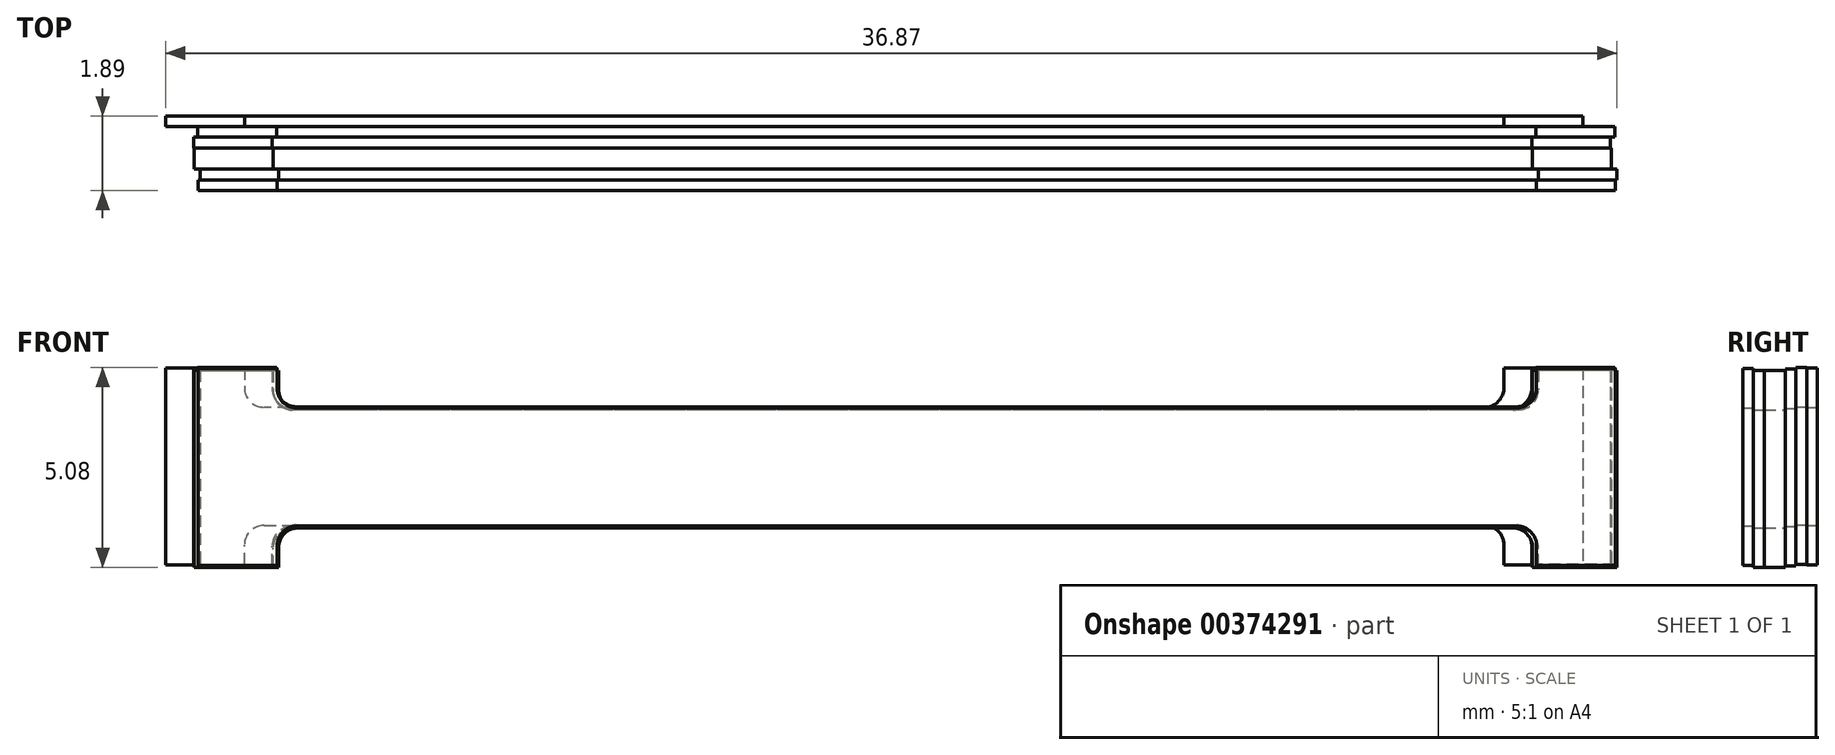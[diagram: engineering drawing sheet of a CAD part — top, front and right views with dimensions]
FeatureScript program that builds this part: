
annotation { "Feature Type Name" : "Feature", "Feature Type Description" : "" }
export const myFeature = defineFeature(function(context is Context, id is Id, definition is map)
    precondition{}
    {
        {
            var Q0;
            Q0=qCreatedBy(makeId("Front.planeOp"),FACE);
            var sketch = newSketch(context, id + "F0", { "sketchPlane" : qUnion([Q0])});
            skLineSegment(sketch, "E0", {"start": v(-18, 2.5) * mm, "end": v(-18, 0) * mm});
            skLineSegment(sketch, "E1", {"start": v(-18, 2.5) * mm, "end": v(-16, 2.5) * mm});
            skLineSegment(sketch, "E2", {"start": v(-18, 0) * mm, "end": v(18, 0) * mm});
            skLineSegment(sketch, "E3", {"start": v(-16, 2.5) * mm, "end": v(-16, 2) * mm});
            skLineSegment(sketch, "E4", {"start": v(-15.5, 1.5) * mm, "end": v(0, 1.5) * mm});
            skPoint(sketch, "E5.visualSharp", {"position": v(-16, 1.5) * mm});
            skArc(sketch, "E5.filletArc", {"start": v(-16, 2) * mm, "mid": v(-15.85, 1.65) * mm, "end": v(-15.5, 1.5) * mm});
            skLineSegment(sketch, "E6.MirrorCS", {"start": v(15.5, 1.5) * mm, "end": v(0, 1.5) * mm});
            skArc(sketch, "E7.MirrorCS", {"start": v(16, 2) * mm, "mid": v(15.85, 1.65) * mm, "end": v(15.5, 1.5) * mm});
            skLineSegment(sketch, "E8.MirrorCS", {"start": v(16, 2.5) * mm, "end": v(16, 2) * mm});
            skLineSegment(sketch, "E9.MirrorCS", {"start": v(18, 2.5) * mm, "end": v(16, 2.5) * mm});
            skLineSegment(sketch, "E10.MirrorCS", {"start": v(18, 2.5) * mm, "end": v(18, 0) * mm});
            skLineSegment(sketch, "E11.MirrorCS", {"start": v(-18, -2.5) * mm, "end": v(-18, 0) * mm});
            skLineSegment(sketch, "E12.MirrorCS", {"start": v(-18, -2.5) * mm, "end": v(-16, -2.5) * mm});
            skLineSegment(sketch, "E13.MirrorCS", {"start": v(-16, -2.5) * mm, "end": v(-16, -2) * mm});
            skArc(sketch, "E14.MirrorCS", {"start": v(-16, -2) * mm, "mid": v(-15.85, -1.65) * mm, "end": v(-15.5, -1.5) * mm});
            skLineSegment(sketch, "E15.MirrorCS", {"start": v(-15.5, -1.5) * mm, "end": v(0, -1.5) * mm});
            skLineSegment(sketch, "E16.MirrorCS", {"start": v(15.5, -1.5) * mm, "end": v(0, -1.5) * mm});
            skArc(sketch, "E17.MirrorCS", {"start": v(16, -2) * mm, "mid": v(15.85, -1.65) * mm, "end": v(15.5, -1.5) * mm});
            skLineSegment(sketch, "E18.MirrorCS", {"start": v(16, -2.5) * mm, "end": v(16, -2) * mm});
            skLineSegment(sketch, "E19.MirrorCS", {"start": v(18, -2.5) * mm, "end": v(16, -2.5) * mm});
            skLineSegment(sketch, "E20.MirrorCS", {"start": v(18, -2.5) * mm, "end": v(18, 0) * mm});
            skSolve(sketch);
        }
        {
            var Q0;
            Q0=qSketchRegion(id+"F0",true);
            extrude(context, id + "F1", {"entities" : qUnion([Q0]), "depth" : 0.27 * mm});
        }
        {
            var Q0;
            Q0=qCreatedBy(makeId("Front.planeOp"),FACE);
            cPlane(context, id + "F2", {"entities" : qUnion([Q0]), "cplaneType" : CPlaneType.OFFSET, "offset" : 0.27 * mm, "width" : 150 * mm, "height" : 150 * mm});
        }
        {
            var Q0;
            Q0=qCreatedBy(id+"F2.planeOp",FACE);
            var sketch = newSketch(context, id + "F3", { "sketchPlane" : qUnion([Q0])});
            skLineSegment(sketch, "E21", {"start": v(-17.18, 2.51) * mm, "end": v(-17.18, 0.01) * mm});
            skLineSegment(sketch, "E22", {"start": v(-17.18, 2.51) * mm, "end": v(-15.18, 2.51) * mm});
            skLineSegment(sketch, "E23", {"start": v(-17.18, 0.01) * mm, "end": v(18.82, 0.01) * mm});
            skLineSegment(sketch, "E24", {"start": v(-15.18, 2.51) * mm, "end": v(-15.18, 2.01) * mm});
            skLineSegment(sketch, "E25", {"start": v(-14.68, 1.51) * mm, "end": v(0.82, 1.51) * mm});
            skPoint(sketch, "E26.visualSharp", {"position": v(-15.18, 1.51) * mm});
            skArc(sketch, "E26.filletArc", {"start": v(-15.18, 2.01) * mm, "mid": v(-15.04, 1.66) * mm, "end": v(-14.68, 1.51) * mm});
            skLineSegment(sketch, "E27.MirrorCS", {"start": v(16.32, 1.51) * mm, "end": v(0.82, 1.51) * mm});
            skArc(sketch, "E28.MirrorCS", {"start": v(16.82, 2.01) * mm, "mid": v(16.67, 1.66) * mm, "end": v(16.32, 1.51) * mm});
            skLineSegment(sketch, "E29.MirrorCS", {"start": v(16.82, 2.51) * mm, "end": v(16.82, 2.01) * mm});
            skLineSegment(sketch, "E30.MirrorCS", {"start": v(18.82, 2.51) * mm, "end": v(16.82, 2.51) * mm});
            skLineSegment(sketch, "E31.MirrorCS", {"start": v(18.82, 2.51) * mm, "end": v(18.82, 0.01) * mm});
            skLineSegment(sketch, "E32.MirrorCS", {"start": v(-17.18, -2.49) * mm, "end": v(-17.18, 0.01) * mm});
            skLineSegment(sketch, "E33.MirrorCS", {"start": v(-17.18, -2.49) * mm, "end": v(-15.18, -2.49) * mm});
            skLineSegment(sketch, "E34.MirrorCS", {"start": v(-15.18, -2.49) * mm, "end": v(-15.18, -1.99) * mm});
            skArc(sketch, "E35.MirrorCS", {"start": v(-15.18, -1.99) * mm, "mid": v(-15.04, -1.63) * mm, "end": v(-14.68, -1.49) * mm});
            skLineSegment(sketch, "E36.MirrorCS", {"start": v(-14.68, -1.49) * mm, "end": v(0.82, -1.49) * mm});
            skLineSegment(sketch, "E37.MirrorCS", {"start": v(16.32, -1.49) * mm, "end": v(0.82, -1.49) * mm});
            skArc(sketch, "E38.MirrorCS", {"start": v(16.82, -1.99) * mm, "mid": v(16.67, -1.63) * mm, "end": v(16.32, -1.49) * mm});
            skLineSegment(sketch, "E39.MirrorCS", {"start": v(16.82, -2.49) * mm, "end": v(16.82, -1.99) * mm});
            skLineSegment(sketch, "E40.MirrorCS", {"start": v(18.82, -2.49) * mm, "end": v(16.82, -2.49) * mm});
            skLineSegment(sketch, "E41.MirrorCS", {"start": v(18.82, -2.49) * mm, "end": v(18.82, 0.01) * mm});
            skSolve(sketch);
        }
        {
            var Q0;
            Q0=qSketchRegion(id+"F3",true);
            extrude(context, id + "F4", {"entities" : qUnion([Q0]), "operationType" : NewBodyOperationType.REMOVE, "depth" : 0.27 * mm});
        }
        {
            var Q0;
            Q0=qCreatedBy(id+"F2.planeOp",FACE);
            cPlane(context, id + "F5", {"entities" : qUnion([Q0]), "cplaneType" : CPlaneType.OFFSET, "offset" : 0.27 * mm, "width" : 150 * mm, "height" : 150 * mm});
        }
        {
            var Q0;
            Q0=qCreatedBy(id+"F5.planeOp",FACE);
            var sketch = newSketch(context, id + "F6", { "sketchPlane" : qUnion([Q0])});
            skLineSegment(sketch, "E42", {"start": v(-17.3, 2.47) * mm, "end": v(-17.3, -0.03) * mm});
            skLineSegment(sketch, "E43", {"start": v(-17.3, 2.47) * mm, "end": v(-15.3, 2.47) * mm});
            skLineSegment(sketch, "E44", {"start": v(-17.3, -0.03) * mm, "end": v(18.7, -0.03) * mm});
            skLineSegment(sketch, "E45", {"start": v(-15.3, 2.47) * mm, "end": v(-15.3, 1.97) * mm});
            skLineSegment(sketch, "E46", {"start": v(-14.8, 1.47) * mm, "end": v(0.7, 1.47) * mm});
            skPoint(sketch, "E47.visualSharp", {"position": v(-15.3, 1.47) * mm});
            skArc(sketch, "E47.filletArc", {"start": v(-15.3, 1.97) * mm, "mid": v(-15.15, 1.62) * mm, "end": v(-14.8, 1.47) * mm});
            skLineSegment(sketch, "E48.MirrorCS", {"start": v(16.2, 1.47) * mm, "end": v(0.7, 1.47) * mm});
            skArc(sketch, "E49.MirrorCS", {"start": v(16.7, 1.97) * mm, "mid": v(16.56, 1.62) * mm, "end": v(16.2, 1.47) * mm});
            skLineSegment(sketch, "E50.MirrorCS", {"start": v(16.7, 2.47) * mm, "end": v(16.7, 1.97) * mm});
            skLineSegment(sketch, "E51.MirrorCS", {"start": v(18.7, 2.47) * mm, "end": v(16.7, 2.47) * mm});
            skLineSegment(sketch, "E52.MirrorCS", {"start": v(18.7, 2.47) * mm, "end": v(18.7, -0.03) * mm});
            skLineSegment(sketch, "E53.MirrorCS", {"start": v(-17.3, -2.53) * mm, "end": v(-17.3, -0.03) * mm});
            skLineSegment(sketch, "E54.MirrorCS", {"start": v(-17.3, -2.53) * mm, "end": v(-15.3, -2.53) * mm});
            skLineSegment(sketch, "E55.MirrorCS", {"start": v(-15.3, -2.53) * mm, "end": v(-15.3, -2.03) * mm});
            skArc(sketch, "E56.MirrorCS", {"start": v(-15.3, -2.03) * mm, "mid": v(-15.15, -1.67) * mm, "end": v(-14.8, -1.53) * mm});
            skLineSegment(sketch, "E57.MirrorCS", {"start": v(-14.8, -1.53) * mm, "end": v(0.7, -1.53) * mm});
            skLineSegment(sketch, "E58.MirrorCS", {"start": v(16.2, -1.53) * mm, "end": v(0.7, -1.53) * mm});
            skArc(sketch, "E59.MirrorCS", {"start": v(16.7, -2.03) * mm, "mid": v(16.56, -1.67) * mm, "end": v(16.2, -1.53) * mm});
            skLineSegment(sketch, "E60.MirrorCS", {"start": v(16.7, -2.53) * mm, "end": v(16.7, -2.03) * mm});
            skLineSegment(sketch, "E61.MirrorCS", {"start": v(18.7, -2.53) * mm, "end": v(16.7, -2.53) * mm});
            skLineSegment(sketch, "E62.MirrorCS", {"start": v(18.7, -2.53) * mm, "end": v(18.7, -0.03) * mm});
            skSolve(sketch);
        }
        {
            var Q0;
            Q0=qSketchRegion(id+"F6",true);
            extrude(context, id + "F7", {"entities" : qUnion([Q0]), "operationType" : NewBodyOperationType.ADD, "depth" : 0.27 * mm});
        }
        {
            var Q0;
            Q0=qCreatedBy(id+"F5.planeOp",FACE);
            cPlane(context, id + "F8", {"entities" : qUnion([Q0]), "cplaneType" : CPlaneType.OFFSET, "offset" : 0.27 * mm, "width" : 150 * mm, "height" : 150 * mm});
        }
        {
            var Q0;
            Q0=qCreatedBy(id+"F8.planeOp",FACE);
            var sketch = newSketch(context, id + "F9", { "sketchPlane" : qUnion([Q0])});
            skLineSegment(sketch, "E63", {"start": v(-17.25, 2.45) * mm, "end": v(-17.25, -0.05) * mm});
            skLineSegment(sketch, "E64", {"start": v(-17.25, 2.45) * mm, "end": v(-15.25, 2.45) * mm});
            skLineSegment(sketch, "E65", {"start": v(-17.25, -0.05) * mm, "end": v(18.75, -0.05) * mm});
            skLineSegment(sketch, "E66", {"start": v(-15.25, 2.45) * mm, "end": v(-15.25, 1.95) * mm});
            skLineSegment(sketch, "E67", {"start": v(-14.75, 1.45) * mm, "end": v(0.75, 1.45) * mm});
            skPoint(sketch, "E68.visualSharp", {"position": v(-15.25, 1.45) * mm});
            skArc(sketch, "E68.filletArc", {"start": v(-15.25, 1.95) * mm, "mid": v(-15.1, 1.6) * mm, "end": v(-14.75, 1.45) * mm});
            skLineSegment(sketch, "E69.MirrorCS", {"start": v(16.25, 1.45) * mm, "end": v(0.75, 1.45) * mm});
            skArc(sketch, "E70.MirrorCS", {"start": v(16.75, 1.95) * mm, "mid": v(16.6, 1.6) * mm, "end": v(16.25, 1.45) * mm});
            skLineSegment(sketch, "E71.MirrorCS", {"start": v(16.75, 2.45) * mm, "end": v(16.75, 1.95) * mm});
            skLineSegment(sketch, "E72.MirrorCS", {"start": v(18.75, 2.45) * mm, "end": v(16.75, 2.45) * mm});
            skLineSegment(sketch, "E73.MirrorCS", {"start": v(18.75, 2.45) * mm, "end": v(18.75, -0.05) * mm});
            skLineSegment(sketch, "E74.MirrorCS", {"start": v(-17.25, -2.55) * mm, "end": v(-17.25, -0.05) * mm});
            skLineSegment(sketch, "E75.MirrorCS", {"start": v(-17.25, -2.55) * mm, "end": v(-15.25, -2.55) * mm});
            skLineSegment(sketch, "E76.MirrorCS", {"start": v(-15.25, -2.55) * mm, "end": v(-15.25, -2.05) * mm});
            skArc(sketch, "E77.MirrorCS", {"start": v(-15.25, -2.05) * mm, "mid": v(-15.1, -1.7) * mm, "end": v(-14.75, -1.55) * mm});
            skLineSegment(sketch, "E78.MirrorCS", {"start": v(-14.75, -1.55) * mm, "end": v(0.75, -1.55) * mm});
            skLineSegment(sketch, "E79.MirrorCS", {"start": v(16.25, -1.55) * mm, "end": v(0.75, -1.55) * mm});
            skArc(sketch, "E80.MirrorCS", {"start": v(16.75, -2.05) * mm, "mid": v(16.6, -1.7) * mm, "end": v(16.25, -1.55) * mm});
            skLineSegment(sketch, "E81.MirrorCS", {"start": v(16.75, -2.55) * mm, "end": v(16.75, -2.05) * mm});
            skLineSegment(sketch, "E82.MirrorCS", {"start": v(18.75, -2.55) * mm, "end": v(16.75, -2.55) * mm});
            skLineSegment(sketch, "E83.MirrorCS", {"start": v(18.75, -2.55) * mm, "end": v(18.75, -0.05) * mm});
            skSolve(sketch);
        }
        {
            var Q0;
            Q0=qSketchRegion(id+"F9",true);
            extrude(context, id + "F10", {"entities" : qUnion([Q0]), "operationType" : NewBodyOperationType.REMOVE, "depth" : 0.27 * mm});
        }
        {
            var Q0;
            Q0=qCreatedBy(id+"F8.planeOp",FACE);
            cPlane(context, id + "F11", {"entities" : qUnion([Q0]), "cplaneType" : CPlaneType.OFFSET, "offset" : 0.27 * mm, "width" : 150 * mm, "height" : 150 * mm});
        }
        {
            var Q0;
            Q0=qCreatedBy(id+"F11.planeOp",FACE);
            var sketch = newSketch(context, id + "F12", { "sketchPlane" : qUnion([Q0])});
            skLineSegment(sketch, "E84", {"start": v(-17.27, 2.43) * mm, "end": v(-17.27, -0.07) * mm});
            skLineSegment(sketch, "E85", {"start": v(-17.27, 2.43) * mm, "end": v(-15.27, 2.43) * mm});
            skLineSegment(sketch, "E86", {"start": v(-17.27, -0.07) * mm, "end": v(18.73, -0.07) * mm});
            skLineSegment(sketch, "E87", {"start": v(-15.27, 2.43) * mm, "end": v(-15.27, 1.93) * mm});
            skLineSegment(sketch, "E88", {"start": v(-14.77, 1.43) * mm, "end": v(0.73, 1.43) * mm});
            skPoint(sketch, "E89.visualSharp", {"position": v(-15.27, 1.43) * mm});
            skArc(sketch, "E89.filletArc", {"start": v(-15.27, 1.93) * mm, "mid": v(-15.13, 1.58) * mm, "end": v(-14.77, 1.43) * mm});
            skLineSegment(sketch, "E90.MirrorCS", {"start": v(16.23, 1.43) * mm, "end": v(0.73, 1.43) * mm});
            skArc(sketch, "E91.MirrorCS", {"start": v(16.73, 1.93) * mm, "mid": v(16.58, 1.58) * mm, "end": v(16.23, 1.43) * mm});
            skLineSegment(sketch, "E92.MirrorCS", {"start": v(16.73, 2.43) * mm, "end": v(16.73, 1.93) * mm});
            skLineSegment(sketch, "E93.MirrorCS", {"start": v(18.73, 2.43) * mm, "end": v(16.73, 2.43) * mm});
            skLineSegment(sketch, "E94.MirrorCS", {"start": v(18.73, 2.43) * mm, "end": v(18.73, -0.07) * mm});
            skLineSegment(sketch, "E95.MirrorCS", {"start": v(-17.27, -2.57) * mm, "end": v(-17.27, -0.07) * mm});
            skLineSegment(sketch, "E96.MirrorCS", {"start": v(-17.27, -2.57) * mm, "end": v(-15.27, -2.57) * mm});
            skLineSegment(sketch, "E97.MirrorCS", {"start": v(-15.27, -2.57) * mm, "end": v(-15.27, -2.07) * mm});
            skArc(sketch, "E98.MirrorCS", {"start": v(-15.27, -2.07) * mm, "mid": v(-15.13, -1.71) * mm, "end": v(-14.77, -1.57) * mm});
            skLineSegment(sketch, "E99.MirrorCS", {"start": v(-14.77, -1.57) * mm, "end": v(0.73, -1.57) * mm});
            skLineSegment(sketch, "E100.MirrorCS", {"start": v(16.23, -1.57) * mm, "end": v(0.73, -1.57) * mm});
            skArc(sketch, "E101.MirrorCS", {"start": v(16.73, -2.07) * mm, "mid": v(16.58, -1.71) * mm, "end": v(16.23, -1.57) * mm});
            skLineSegment(sketch, "E102.MirrorCS", {"start": v(16.73, -2.57) * mm, "end": v(16.73, -2.07) * mm});
            skLineSegment(sketch, "E103.MirrorCS", {"start": v(18.73, -2.57) * mm, "end": v(16.73, -2.57) * mm});
            skLineSegment(sketch, "E104.MirrorCS", {"start": v(18.73, -2.57) * mm, "end": v(18.73, -0.07) * mm});
            skSolve(sketch);
        }
        {
            var Q0;
            Q0=qSketchRegion(id+"F12",true);
            extrude(context, id + "F13", {"entities" : qUnion([Q0]), "operationType" : NewBodyOperationType.ADD, "depth" : 0.27 * mm});
        }
        {
            var Q0;
            Q0=qSketchRegion(id+"F3",true);
            extrude(context, id + "F14", {"entities" : qUnion([Q0]), "depth" : 0.27 * mm});
        }
        {
            var Q0;
            Q0=qSketchRegion(id+"F12",true);
            extrude(context, id + "F15", {"entities" : qUnion([Q0]), "operationType" : NewBodyOperationType.ADD, "oppositeDirection" : true, "depth" : 0.27 * mm});
        }
        {
            var Q0;
            Q0=qCreatedBy(id+"F11.planeOp",FACE);
            cPlane(context, id + "F16", {"entities" : qUnion([Q0]), "cplaneType" : CPlaneType.OFFSET, "offset" : 0.27 * mm, "width" : 150 * mm, "height" : 150 * mm});
        }
        {
            var Q0;
            Q0=qCreatedBy(id+"F16.planeOp",FACE);
            var sketch = newSketch(context, id + "F17", { "sketchPlane" : qUnion([Q0])});
            skLineSegment(sketch, "E105", {"start": v(-17.13, 2.44) * mm, "end": v(-17.13, -0.06) * mm});
            skLineSegment(sketch, "E106", {"start": v(-17.13, 2.44) * mm, "end": v(-15.13, 2.44) * mm});
            skLineSegment(sketch, "E107", {"start": v(-17.13, -0.06) * mm, "end": v(18.87, -0.06) * mm});
            skLineSegment(sketch, "E108", {"start": v(-15.13, 2.44) * mm, "end": v(-15.13, 1.94) * mm});
            skLineSegment(sketch, "E109", {"start": v(-14.63, 1.44) * mm, "end": v(0.87, 1.44) * mm});
            skPoint(sketch, "E110.visualSharp", {"position": v(-15.13, 1.44) * mm});
            skArc(sketch, "E110.filletArc", {"start": v(-15.13, 1.94) * mm, "mid": v(-14.98, 1.58) * mm, "end": v(-14.63, 1.44) * mm});
            skLineSegment(sketch, "E111.MirrorCS", {"start": v(16.37, 1.44) * mm, "end": v(0.87, 1.44) * mm});
            skArc(sketch, "E112.MirrorCS", {"start": v(16.87, 1.94) * mm, "mid": v(16.73, 1.58) * mm, "end": v(16.37, 1.44) * mm});
            skLineSegment(sketch, "E113.MirrorCS", {"start": v(16.87, 2.44) * mm, "end": v(16.87, 1.94) * mm});
            skLineSegment(sketch, "E114.MirrorCS", {"start": v(18.87, 2.44) * mm, "end": v(16.87, 2.44) * mm});
            skLineSegment(sketch, "E115.MirrorCS", {"start": v(18.87, 2.44) * mm, "end": v(18.87, -0.06) * mm});
            skLineSegment(sketch, "E116.MirrorCS", {"start": v(-17.13, -2.56) * mm, "end": v(-17.13, -0.06) * mm});
            skLineSegment(sketch, "E117.MirrorCS", {"start": v(-17.13, -2.56) * mm, "end": v(-15.13, -2.56) * mm});
            skLineSegment(sketch, "E118.MirrorCS", {"start": v(-15.13, -2.56) * mm, "end": v(-15.13, -2.06) * mm});
            skArc(sketch, "E119.MirrorCS", {"start": v(-15.13, -2.06) * mm, "mid": v(-14.98, -1.7) * mm, "end": v(-14.63, -1.56) * mm});
            skLineSegment(sketch, "E120.MirrorCS", {"start": v(-14.63, -1.56) * mm, "end": v(0.87, -1.56) * mm});
            skLineSegment(sketch, "E121.MirrorCS", {"start": v(16.37, -1.56) * mm, "end": v(0.87, -1.56) * mm});
            skArc(sketch, "E122.MirrorCS", {"start": v(16.87, -2.06) * mm, "mid": v(16.73, -1.7) * mm, "end": v(16.37, -1.56) * mm});
            skLineSegment(sketch, "E123.MirrorCS", {"start": v(16.87, -2.56) * mm, "end": v(16.87, -2.06) * mm});
            skLineSegment(sketch, "E124.MirrorCS", {"start": v(18.87, -2.56) * mm, "end": v(16.87, -2.56) * mm});
            skLineSegment(sketch, "E125.MirrorCS", {"start": v(18.87, -2.56) * mm, "end": v(18.87, -0.06) * mm});
            skSolve(sketch);
        }
        {
            var Q0;
            Q0 = qSketchRegion(id + "F17", true);
            extrude(context, id + "F18", {"entities" : qUnion([Q0]), "depth" : 0.27 * mm});
        }
        {
            var Q0;
            Q0=qCreatedBy(id+"F16.planeOp",FACE);
            cPlane(context, id + "F19", {"entities" : qUnion([Q0]), "cplaneType" : CPlaneType.OFFSET, "offset" : 0.27 * mm, "width" : 150 * mm, "height" : 150 * mm});
        }
        {
            var Q0;
            Q0=qCreatedBy(id+"F19.planeOp",FACE);
            var sketch = newSketch(context, id + "F20", { "sketchPlane" : qUnion([Q0])});
            skLineSegment(sketch, "E126", {"start": v(-17.17, 2.48) * mm, "end": v(-17.17, -0.02) * mm});
            skLineSegment(sketch, "E127", {"start": v(-17.17, 2.48) * mm, "end": v(-15.17, 2.48) * mm});
            skLineSegment(sketch, "E128", {"start": v(-17.17, -0.02) * mm, "end": v(18.83, -0.02) * mm});
            skLineSegment(sketch, "E129", {"start": v(-15.17, 2.48) * mm, "end": v(-15.17, 1.98) * mm});
            skLineSegment(sketch, "E130", {"start": v(-14.67, 1.48) * mm, "end": v(0.83, 1.48) * mm});
            skPoint(sketch, "E131.visualSharp", {"position": v(-15.17, 1.48) * mm});
            skArc(sketch, "E131.filletArc", {"start": v(-15.17, 1.98) * mm, "mid": v(-15.02, 1.63) * mm, "end": v(-14.67, 1.48) * mm});
            skLineSegment(sketch, "E132.MirrorCS", {"start": v(16.33, 1.48) * mm, "end": v(0.83, 1.48) * mm});
            skArc(sketch, "E133.MirrorCS", {"start": v(16.83, 1.98) * mm, "mid": v(16.68, 1.63) * mm, "end": v(16.33, 1.48) * mm});
            skLineSegment(sketch, "E134.MirrorCS", {"start": v(16.83, 2.48) * mm, "end": v(16.83, 1.98) * mm});
            skLineSegment(sketch, "E135.MirrorCS", {"start": v(18.83, 2.48) * mm, "end": v(16.83, 2.48) * mm});
            skLineSegment(sketch, "E136.MirrorCS", {"start": v(18.83, 2.48) * mm, "end": v(18.83, -0.02) * mm});
            skLineSegment(sketch, "E137.MirrorCS", {"start": v(-17.17, -2.52) * mm, "end": v(-17.17, -0.02) * mm});
            skLineSegment(sketch, "E138.MirrorCS", {"start": v(-17.17, -2.52) * mm, "end": v(-15.17, -2.52) * mm});
            skLineSegment(sketch, "E139.MirrorCS", {"start": v(-15.17, -2.52) * mm, "end": v(-15.17, -2.02) * mm});
            skArc(sketch, "E140.MirrorCS", {"start": v(-15.17, -2.02) * mm, "mid": v(-15.02, -1.67) * mm, "end": v(-14.67, -1.52) * mm});
            skLineSegment(sketch, "E141.MirrorCS", {"start": v(-14.67, -1.52) * mm, "end": v(0.83, -1.52) * mm});
            skLineSegment(sketch, "E142.MirrorCS", {"start": v(16.33, -1.52) * mm, "end": v(0.83, -1.52) * mm});
            skArc(sketch, "E143.MirrorCS", {"start": v(16.83, -2.02) * mm, "mid": v(16.68, -1.67) * mm, "end": v(16.33, -1.52) * mm});
            skLineSegment(sketch, "E144.MirrorCS", {"start": v(16.83, -2.52) * mm, "end": v(16.83, -2.02) * mm});
            skLineSegment(sketch, "E145.MirrorCS", {"start": v(18.83, -2.52) * mm, "end": v(16.83, -2.52) * mm});
            skLineSegment(sketch, "E146.MirrorCS", {"start": v(18.83, -2.52) * mm, "end": v(18.83, -0.02) * mm});
            skSolve(sketch);
        }
        {
            var Q0;
            Q0 = qSketchRegion(id + "F20", true);
            extrude(context, id + "F21", {"entities" : qUnion([Q0]), "operationType" : NewBodyOperationType.ADD, "depth" : 0.27 * mm});
        }
    });
